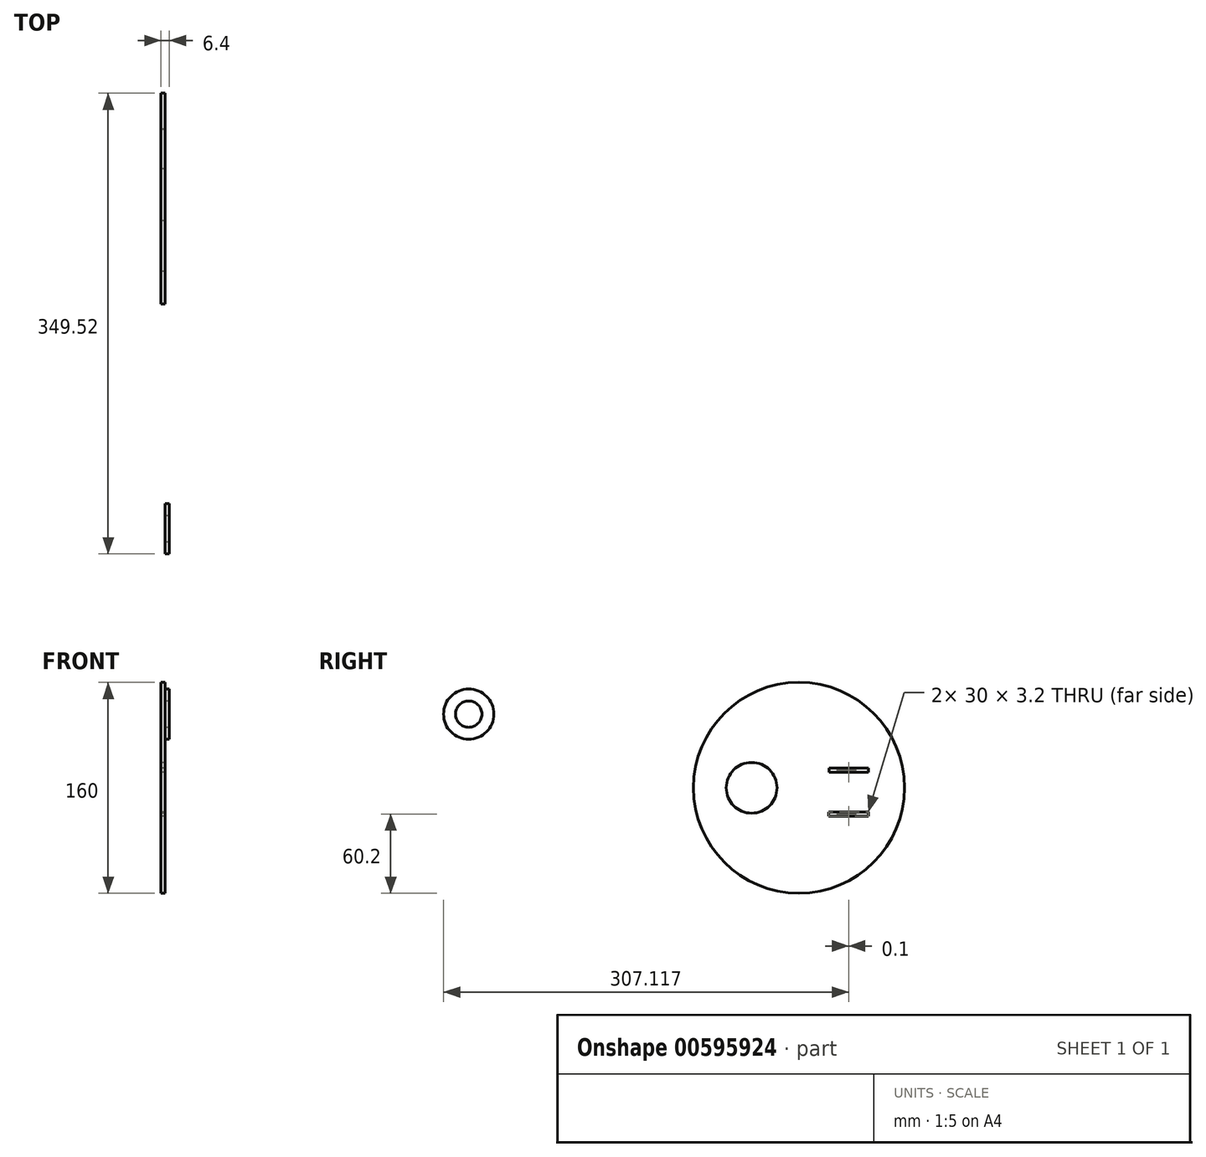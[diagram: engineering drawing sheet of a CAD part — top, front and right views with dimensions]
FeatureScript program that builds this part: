
annotation { "Feature Type Name" : "Feature", "Feature Type Description" : "" }
export const myFeature = defineFeature(function(context is Context, id is Id, definition is map)
    precondition{}
    {
        {
            var Q0;
            Q0=qCreatedBy(makeId("Right.planeOp"),FACE);
            var sketch = newSketch(context, id + "F0", { "sketchPlane" : qUnion([Q0])});
            skCircle(sketch, "E0", {"center": v(0, 0) * mm, "radius": 80 * mm});
            skLineSegment(sketch, "E1.bottom", {"start": v(22.7, 15) * mm, "end": v(52.7, 15) * mm});
            skLineSegment(sketch, "E1.top", {"start": v(22.7, 11.8) * mm, "end": v(52.7, 11.8) * mm});
            skLineSegment(sketch, "E1.left", {"start": v(22.7, 15) * mm, "end": v(22.7, 11.8) * mm});
            skLineSegment(sketch, "E1.right", {"start": v(52.7, 15) * mm, "end": v(52.7, 11.8) * mm});
            skLineSegment(sketch, "E2.bottom", {"start": v(22.6, -18.2) * mm, "end": v(52.6, -18.2) * mm});
            skLineSegment(sketch, "E2.top", {"start": v(22.6, -21.4) * mm, "end": v(52.6, -21.4) * mm});
            skLineSegment(sketch, "E2.left", {"start": v(22.6, -18.2) * mm, "end": v(22.6, -21.4) * mm});
            skLineSegment(sketch, "E2.right", {"start": v(52.6, -18.2) * mm, "end": v(52.6, -21.4) * mm});
            skCircle(sketch, "E3", {"center": v(-35.92, 0) * mm, "radius": 19.25 * mm});
            skLineSegment(sketch, "E4", {"start": v(52.7, 11.8) * mm, "end": v(52.7, 11.8) * mm});
            skSolve(sketch);
        }
        {
            var Q0;
            Q0=makeQuery(id+"F0.imprint","IMPRINT",FACE,{"disambiguationData":[TD([[makeQuery(id+"F0.imprint","IMPRINT",EDGE,{"derivedFrom":sQuery(id+"F0.wireOp",EDGE,"E0")}),1.0]])]});
            extrude(context, id + "F1", {"entities" : qUnion([Q0]), "depth" : 3.2 * mm, "offsetDistance" : 25 * mm});
        }
        {
            var Q0;
            Q0=makeQuery(id+"F1.opExtrude","CAP_FACE",FACE,{"disambiguationData":[OSD([sQuery(id+"F0.wireOp",EDGE,"E0"),sQuery(id+"F0.wireOp",EDGE,"E1.bottom"),sQuery(id+"F0.wireOp",EDGE,"E1.top"),sQuery(id+"F0.wireOp",EDGE,"E1.left"),sQuery(id+"F0.wireOp",EDGE,"E1.right"),sQuery(id+"F0.wireOp",EDGE,"E2.bottom"),sQuery(id+"F0.wireOp",EDGE,"E2.top"),sQuery(id+"F0.wireOp",EDGE,"E2.left"),sQuery(id+"F0.wireOp",EDGE,"E2.right"),sQuery(id+"F0.wireOp",EDGE,"E3")])],"isStart":false});
            var sketch = newSketch(context, id + "F2", { "sketchPlane" : qUnion([Q0])});
            skCircle(sketch, "E5", {"center": v(-250.47, 55.92) * mm, "radius": 19.05 * mm});
            skCircle(sketch, "E6", {"center": v(-250.47, 55.92) * mm, "radius": 10 * mm});
            skSolve(sketch);
        }
        {
            var Q0;
            Q0=qSketchRegion(id+"F2",true);
            extrude(context, id + "F3", {"entities" : qUnion([Q0]), "depth" : 3.2 * mm, "offsetDistance" : 25 * mm});
        }
    });
